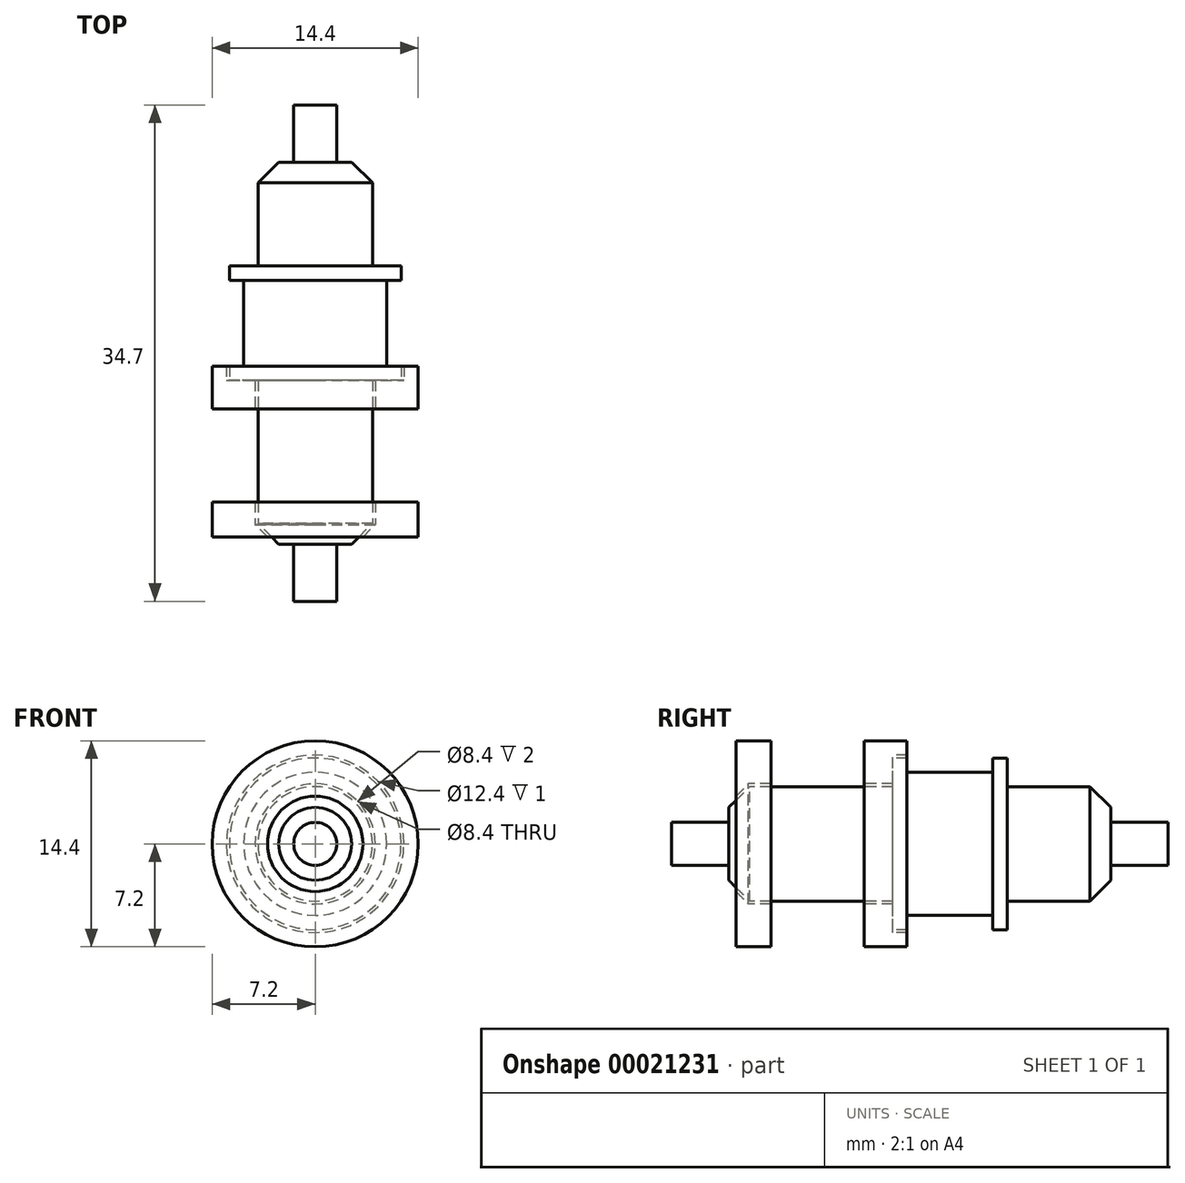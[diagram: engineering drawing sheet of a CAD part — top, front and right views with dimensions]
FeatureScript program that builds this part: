
annotation { "Feature Type Name" : "Feature", "Feature Type Description" : "" }
export const myFeature = defineFeature(function(context is Context, id is Id, definition is map)
    precondition{}
    {
        {
            var Q0;
            Q0=qCreatedBy(makeId("Top.planeOp"),FACE);
            var sketch = newSketch(context, id + "F0", { "sketchPlane" : qUnion([Q0])});
            skLineSegment(sketch, "E0", {"start": v(0, 34.7) * mm, "end": v(1.5, 34.7) * mm});
            skLineSegment(sketch, "E1", {"start": v(1.5, 34.7) * mm, "end": v(1.5, 30.7) * mm});
            skLineSegment(sketch, "E2", {"start": v(1.5, 30.7) * mm, "end": v(2.55, 30.7) * mm});
            skLineSegment(sketch, "E3", {"start": v(2.55, 30.7) * mm, "end": v(4, 29.25) * mm});
            skLineSegment(sketch, "E4", {"start": v(4, 29.25) * mm, "end": v(4, 23.45) * mm});
            skLineSegment(sketch, "E5", {"start": v(4, 23.45) * mm, "end": v(6, 23.45) * mm});
            skLineSegment(sketch, "E6", {"start": v(6, 23.45) * mm, "end": v(6, 22.45) * mm});
            skLineSegment(sketch, "E7", {"start": v(6, 22.45) * mm, "end": v(5, 22.45) * mm});
            skLineSegment(sketch, "E8", {"start": v(5, 22.45) * mm, "end": v(5, 16.45) * mm});
            skLineSegment(sketch, "E9", {"start": v(5, 16.45) * mm, "end": v(6, 16.45) * mm});
            skLineSegment(sketch, "E10", {"start": v(6, 16.45) * mm, "end": v(6, 15.45) * mm});
            skLineSegment(sketch, "E11", {"start": v(6, 15.45) * mm, "end": v(4, 15.45) * mm});
            skLineSegment(sketch, "E12", {"start": v(4, 15.45) * mm, "end": v(4, 5.45) * mm});
            skLineSegment(sketch, "E13", {"start": v(4, 5.45) * mm, "end": v(2.55, 4) * mm});
            skLineSegment(sketch, "E14", {"start": v(2.55, 4) * mm, "end": v(1.5, 4) * mm});
            skLineSegment(sketch, "E15", {"start": v(1.5, 4) * mm, "end": v(1.5, 0) * mm});
            skLineSegment(sketch, "E16", {"start": v(1.5, 0) * mm, "end": v(0, 0) * mm});
            skLineSegment(sketch, "E17", {"start": v(0, 0) * mm, "end": v(0, 34.7) * mm});
            skLineSegment(sketch, "E18", {"start": v(4.2, 15.45) * mm, "end": v(4.2, 13.45) * mm});
            skLineSegment(sketch, "E19", {"start": v(4.2, 13.45) * mm, "end": v(7.2, 13.45) * mm});
            skLineSegment(sketch, "E20", {"start": v(4.2, 15.45) * mm, "end": v(6.2, 15.45) * mm});
            skLineSegment(sketch, "E21", {"start": v(6.2, 15.45) * mm, "end": v(6.2, 16.45) * mm});
            skLineSegment(sketch, "E22", {"start": v(6.2, 16.45) * mm, "end": v(7.2, 16.45) * mm});
            skLineSegment(sketch, "E23", {"start": v(7.2, 16.45) * mm, "end": v(7.2, 13.45) * mm});
            skLineSegment(sketch, "E24", {"start": v(4.2, 6.95) * mm, "end": v(7.2, 6.95) * mm});
            skLineSegment(sketch, "E25", {"start": v(7.2, 6.95) * mm, "end": v(7.2, 4.5) * mm});
            skLineSegment(sketch, "E26", {"start": v(7.2, 4.5) * mm, "end": v(3.33, 4.5) * mm});
            skLineSegment(sketch, "E27", {"start": v(3.33, 4.5) * mm, "end": v(4.2, 5.37) * mm});
            skLineSegment(sketch, "E28", {"start": v(4.2, 5.37) * mm, "end": v(4.2, 6.95) * mm});
            skSolve(sketch);
        }
        {
            var Q0;
            Q0=makeQuery(id+"F0.imprint","IMPRINT",FACE,{"disambiguationData":[TD([[makeQuery(id+"F0.imprint","IMPRINT",EDGE,{"derivedFrom":sQuery(id+"F0.wireOp",EDGE,"E0")}),-1.0]])]});
            var Q1;
            Q1=sQuery(id+"F0.wireOp",EDGE,"E17");
            revolve(context, id + "F1", {"entities" : qUnion([Q0]), "axis" : qUnion([Q1]), "revolveType" : RevolveType.FULL});
        }
        {
            var Q0;
            {var subQ3=sQuery(id+"F0.wireOp",EDGE,"E18");Q0=makeQuery(id+"F0.imprint","IMPRINT",FACE,{"disambiguationData":[TD([[makeQuery(id+"F0.imprint","IMPRINT",EDGE,{"derivedFrom":subQ3}),1.0]])]});}
            var Q1;
            Q1=sQuery(id+"F0.wireOp",EDGE,"E17");
            revolve(context, id + "F2", {"entities" : qUnion([Q0]), "axis" : qUnion([Q1]), "revolveType" : RevolveType.FULL});
        }
        {
            var Q0;
            Q0=makeQuery(id+"F0.imprint","IMPRINT",FACE,{"disambiguationData":[TD([[makeQuery(id+"F0.imprint","IMPRINT",EDGE,{"derivedFrom":sQuery(id+"F0.wireOp",EDGE,"E24")}),-1.0]])]});
            var Q1;
            Q1=sQuery(id+"F0.wireOp",EDGE,"E17");
            revolve(context, id + "F3", {"entities" : qUnion([Q0]), "axis" : qUnion([Q1]), "revolveType" : RevolveType.FULL});
        }
    });
